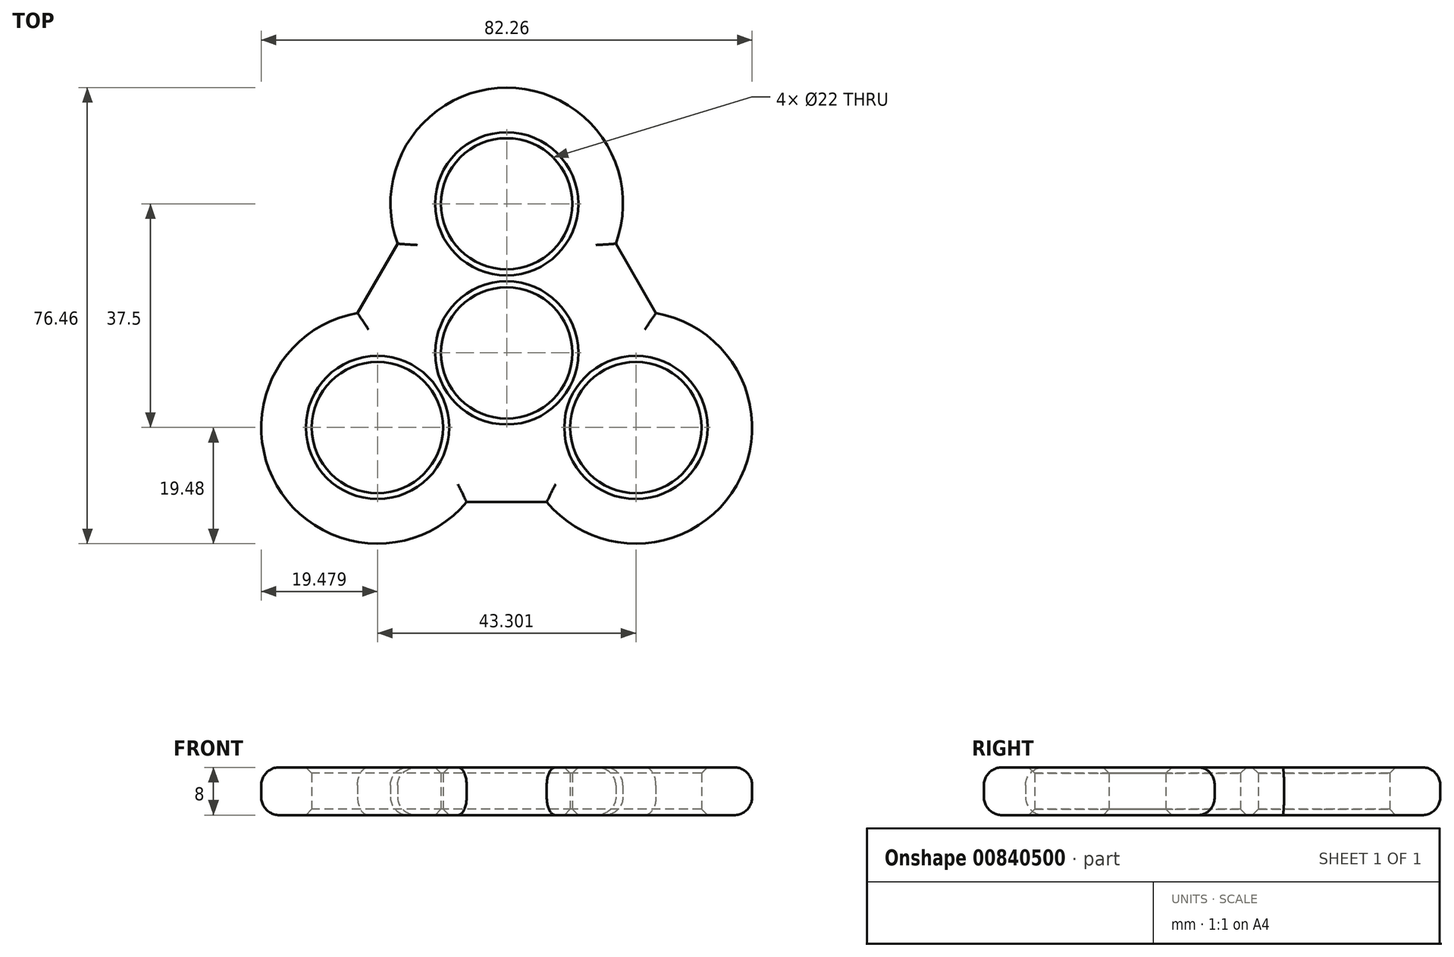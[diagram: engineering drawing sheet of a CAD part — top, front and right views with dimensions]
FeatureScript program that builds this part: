
annotation { "Feature Type Name" : "Feature", "Feature Type Description" : "" }
export const myFeature = defineFeature(function(context is Context, id is Id, definition is map)
    precondition{}
    {
        {
            var Q0;
            Q0=qCreatedBy(makeId("Top.planeOp"),FACE);
            var sketch = newSketch(context, id + "F0", { "sketchPlane" : qUnion([Q0])});
            skCircle(sketch, "E0", {"center": v(0, 25) * mm, "radius": 11 * mm});
            skArc(sketch, "E1.0", {"start": v(18.3, 18.31) * mm, "mid": v(0, 44.48) * mm, "end": v(-18.3, 18.31) * mm});
            skCircle(sketch, "E2.1.0", {"center": v(-21.65, -12.5) * mm, "radius": 11 * mm});
            skArc(sketch, "E2.1.1", {"start": v(-25, 6.69) * mm, "mid": v(-38.52, -22.24) * mm, "end": v(-6.71, -25) * mm});
            skCircle(sketch, "E2.2.0", {"center": v(21.65, -12.5) * mm, "radius": 11 * mm});
            skArc(sketch, "E2.2.1", {"start": v(6.71, -25) * mm, "mid": v(38.52, -22.24) * mm, "end": v(25, 6.69) * mm});
            skPoint(sketch, "E2.center", {"position": v(0, 0) * mm});
            skLineSegment(sketch, "E3.1", {"start": v(18.3, 18.31) * mm, "end": v(25, 6.69) * mm});
            skLineSegment(sketch, "E3.3", {"start": v(6.71, -25) * mm, "end": v(-6.71, -25) * mm});
            skLineSegment(sketch, "E3.5", {"start": v(-25, 6.69) * mm, "end": v(-18.3, 18.31) * mm});
            skPoint(sketch, "E4.orphan", {"position": v(-14.43, -25) * mm});
            skPoint(sketch, "E5.trimOffspring.end.orphan", {"position": v(14.43, 25) * mm});
            skPoint(sketch, "E6.orphan", {"position": v(-14.43, 25) * mm});
            skCircle(sketch, "E7", {"center": v(0, 0) * mm, "radius": 11 * mm});
            skSolve(sketch);
        }
        {
            var Q0;
            Q0=makeQuery(id+"F0.imprint","IMPRINT",FACE,{"disambiguationData":[TD([[makeQuery(id+"F0.imprint","IMPRINT",EDGE,{"derivedFrom":sQuery(id+"F0.wireOp",EDGE,"E0")}),-1.0]])]});
            extrude(context, id + "F1", {"entities" : qUnion([Q0]), "endBound" : BoundingType.SYMMETRIC, "depth" : 8 * mm, "offsetDistance" : 25 * mm});
        }
        {
            var Q0;
            Q0=makeQuery(id+"F1.opExtrude","CAP_EDGE",EDGE,{"disambiguationData":[OSD([sQuery(id+"F0.wireOp",EDGE,"E2.2.1")])],"isStart":false});
            var Q1;
            Q1=makeQuery(id+"F1.opExtrude","CAP_EDGE",EDGE,{"disambiguationData":[OSD([sQuery(id+"F0.wireOp",EDGE,"E3.1")])],"isStart":false});
            var Q2;
            Q2=makeQuery(id+"F1.opExtrude","CAP_EDGE",EDGE,{"disambiguationData":[OSD([sQuery(id+"F0.wireOp",EDGE,"E1.0")])],"isStart":false});
            var Q3;
            Q3=makeQuery(id+"F1.opExtrude","CAP_EDGE",EDGE,{"disambiguationData":[OSD([sQuery(id+"F0.wireOp",EDGE,"E3.5")])],"isStart":false});
            var Q4;
            Q4=makeQuery(id+"F1.opExtrude","CAP_EDGE",EDGE,{"disambiguationData":[OSD([sQuery(id+"F0.wireOp",EDGE,"E2.1.1")])],"isStart":false});
            var Q5;
            Q5=makeQuery(id+"F1.opExtrude","CAP_EDGE",EDGE,{"disambiguationData":[OSD([sQuery(id+"F0.wireOp",EDGE,"E3.3")])],"isStart":false});
            var Q6;
            Q6=makeQuery(id+"F1.opExtrude","CAP_EDGE",EDGE,{"disambiguationData":[OSD([sQuery(id+"F0.wireOp",EDGE,"E1.0")])],"isStart":true});
            var Q7;
            Q7=makeQuery(id+"F1.opExtrude","CAP_EDGE",EDGE,{"disambiguationData":[OSD([sQuery(id+"F0.wireOp",EDGE,"E2.1.1")])],"isStart":true});
            var Q8;
            Q8=makeQuery(id+"F1.opExtrude","CAP_EDGE",EDGE,{"disambiguationData":[OSD([sQuery(id+"F0.wireOp",EDGE,"E3.3")])],"isStart":true});
            var Q9;
            Q9=makeQuery(id+"F1.opExtrude","CAP_EDGE",EDGE,{"disambiguationData":[OSD([sQuery(id+"F0.wireOp",EDGE,"E2.2.1")])],"isStart":true});
            var Q10;
            Q10=makeQuery(id+"F1.opExtrude","CAP_EDGE",EDGE,{"disambiguationData":[OSD([sQuery(id+"F0.wireOp",EDGE,"E3.1")])],"isStart":true});
            var Q11;
            Q11=makeQuery(id+"F1.opExtrude","CAP_EDGE",EDGE,{"disambiguationData":[OSD([sQuery(id+"F0.wireOp",EDGE,"E3.5")])],"isStart":true});
            fillet(context, id + "F2", {"entities" : qUnion([Q0, Q1, Q2, Q3, Q4, Q5, Q6, Q7, Q8, Q9, Q10, Q11]), "radius" : 3 * mm, "tangentPropagation" : true, "allowEdgeOverflow" : false});
        }
        {
            var Q0;
            Q0=makeQuery(id+"F1.opExtrude","CAP_EDGE",EDGE,{"disambiguationData":[OSD([sQuery(id+"F0.wireOp",EDGE,"E0")])],"isStart":false});
            var Q1;
            Q1=makeQuery(id+"F1.opExtrude","CAP_EDGE",EDGE,{"disambiguationData":[OSD([sQuery(id+"F0.wireOp",EDGE,"E7")])],"isStart":false});
            var Q2;
            Q2=makeQuery(id+"F1.opExtrude","CAP_EDGE",EDGE,{"disambiguationData":[OSD([sQuery(id+"F0.wireOp",EDGE,"E2.1.0")])],"isStart":false});
            var Q3;
            Q3=makeQuery(id+"F1.opExtrude","CAP_EDGE",EDGE,{"disambiguationData":[OSD([sQuery(id+"F0.wireOp",EDGE,"E2.2.0")])],"isStart":false});
            chamfer(context, id + "F3", {"entities" : qUnion([Q0, Q1, Q2, Q3]), "width" : 1 * mm, "tangentPropagation" : true});
        }
        {
            var Q0;
            Q0=makeQuery(id+"F1.opExtrude","CAP_EDGE",EDGE,{"disambiguationData":[OSD([sQuery(id+"F0.wireOp",EDGE,"E2.1.0")])],"isStart":true});
            var Q1;
            Q1=makeQuery(id+"F1.opExtrude","CAP_EDGE",EDGE,{"disambiguationData":[OSD([sQuery(id+"F0.wireOp",EDGE,"E7")])],"isStart":true});
            var Q2;
            Q2=makeQuery(id+"F1.opExtrude","CAP_EDGE",EDGE,{"disambiguationData":[OSD([sQuery(id+"F0.wireOp",EDGE,"E2.2.0")])],"isStart":true});
            var Q3;
            Q3=makeQuery(id+"F1.opExtrude","CAP_EDGE",EDGE,{"disambiguationData":[OSD([sQuery(id+"F0.wireOp",EDGE,"E0")])],"isStart":true});
            chamfer(context, id + "F4", {"entities" : qUnion([Q0, Q1, Q2, Q3]), "width" : 1 * mm, "tangentPropagation" : true});
        }
        {
            var Q0;
            Q0=qCreatedBy(makeId("Front.planeOp"),FACE);
            var sketch = newSketch(context, id + "F5", { "sketchPlane" : qUnion([Q0])});
            skLineSegment(sketch, "E8", {"start": v(-28, 14.28) * mm, "end": v(0, 14.28) * mm});
            skLineSegment(sketch, "E9", {"start": v(0, 14.28) * mm, "end": v(0, 0) * mm});
            skLineSegment(sketch, "E10", {"start": v(0, 0) * mm, "end": v(0, -14.28) * mm});
            skLineSegment(sketch, "E11", {"start": v(0, -14.28) * mm, "end": v(-28, -14.28) * mm});
            skArc(sketch, "E12", {"start": v(-10.73, 5.93) * mm, "mid": v(-18.41, 12.08) * mm, "end": v(-28, 14.28) * mm});
            skArc(sketch, "E13", {"start": v(-28, -14.28) * mm, "mid": v(-17.05, -11.37) * mm, "end": v(-9, -3.4) * mm});
            skLineSegment(sketch, "E14", {"start": v(-10.73, 5.93) * mm, "end": v(-9, -3.4) * mm});
            skLineSegment(sketch, "E15", {"start": v(-9, -3.4) * mm, "end": v(0, -3.4) * mm});
            skSolve(sketch);
        }
        {
            var Q0;
            Q0=makeQuery(id+"F5.imprint","IMPRINT",FACE,{"disambiguationData":[TD([[makeQuery(id+"F5.imprint","IMPRINT",EDGE,{"derivedFrom":sQuery(id+"F5.wireOp",EDGE,"E8")}),-1.0]])]});
            var Q1;
            Q1=sQuery(id+"F5.wireOp",EDGE,"E9");
            revolve(context, id + "F6", {"surfaceOperationType" : NewSurfaceOperationType.NEW, "entities" : qUnion([Q0]), "axis" : qUnion([Q1]), "revolveType" : RevolveType.FULL});
        }
        {
            var Q0;
            Q0=makeQuery(id+"F6.opRevolve","SWEPT_EDGE",EDGE,{"disambiguationData":[OSD([sQuery(id+"F5.wireOp",EDGE,"E8"),sQuery(id+"F5.wireOp",EDGE,"E12")])]});
            var Q1;
            Q1=makeQuery(id+"F6.opRevolve","SWEPT_EDGE",EDGE,{"disambiguationData":[OSD([sQuery(id+"F5.wireOp",EDGE,"E11"),sQuery(id+"F5.wireOp",EDGE,"E13")])]});
            fillet(context, id + "F7", {"entities" : qUnion([Q0, Q1]), "radius" : 2 * mm, "tangentPropagation" : true, "allowEdgeOverflow" : false});
        }
        {
            var Q0;
            Q0=makeQuery(id+"F6.opRevolve","SWEPT_BODY",BODY,{"disambiguationData":[OSD([sQuery(id+"F5.wireOp",EDGE,"E8"),sQuery(id+"F5.wireOp",EDGE,"E9"),sQuery(id+"F5.wireOp",EDGE,"E10"),sQuery(id+"F5.wireOp",EDGE,"E12"),sQuery(id+"F5.wireOp",EDGE,"E14"),sQuery(id+"F5.wireOp",EDGE,"E15")])]});
            deleteBodies(context, id + "F8", {"entities" : qUnion([Q0])});
        }
        {
            var Q0;
            Q0=qCreatedBy(makeId("Top.planeOp"),FACE);
            var sketch = newSketch(context, id + "F9", { "sketchPlane" : qUnion([Q0])});
            skLineSegment(sketch, "E16.bottom", {"start": v(-37.7, -50.16) * mm, "end": v(-19.34, -50.16) * mm});
            skLineSegment(sketch, "E16.top", {"start": v(-37.7, -68.4) * mm, "end": v(-19.34, -68.4) * mm});
            skLineSegment(sketch, "E16.left", {"start": v(-37.7, -50.16) * mm, "end": v(-37.7, -68.4) * mm});
            skLineSegment(sketch, "E16.right", {"start": v(-19.34, -50.16) * mm, "end": v(-19.34, -68.4) * mm});
            skSolve(sketch);
        }
        {
            var Q0;
            Q0 = qSketchRegion(id + "F9", true);
            extrude(context, id + "F10", {"entities" : qUnion([Q0]), "depth" : 25 * mm, "offsetDistance" : 25 * mm});
        }
        {
            var Q0;
            Q0=makeQuery(id+"F10.opExtrude","SWEPT_BODY",BODY,{"disambiguationData":[OSD([sQuery(id+"F9.wireOp",EDGE,"E16.bottom"),sQuery(id+"F9.wireOp",EDGE,"E16.top"),sQuery(id+"F9.wireOp",EDGE,"E16.left"),sQuery(id+"F9.wireOp",EDGE,"E16.right")])]});
            deleteBodies(context, id + "F11", {"entities" : qUnion([Q0])});
        }
    });
